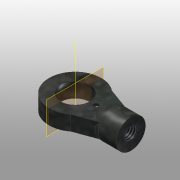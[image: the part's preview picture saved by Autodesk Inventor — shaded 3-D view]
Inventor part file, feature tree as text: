
AUTODESK INVENTOR PART (.ipt)
format: ipt  version: 2015 (Build 190159000, 159)  size: 144,896 bytes
history: native  units: mm
features: other x4, sketch x4, plane x1
ambient origin geometry x8: Origin, YZ Plane, XZ Plane, XY Plane, X Axis, Y Axis, Z Axis, Center Point
bodies: Solid1 (feature_tree)
feature tree (9):
  other  "500-103.ipt"
  other  "Solid1::500-103.ipt"
  other  "TaggingFeature1"
  sketch  "Sketch1"  dims[d0=10.0mm]
  sketch  "Sketch2"
  sketch  "Sketch3"
  sketch  "Sketch4"
  plane  "Work Plane1"
  other  "Work Axis1"
